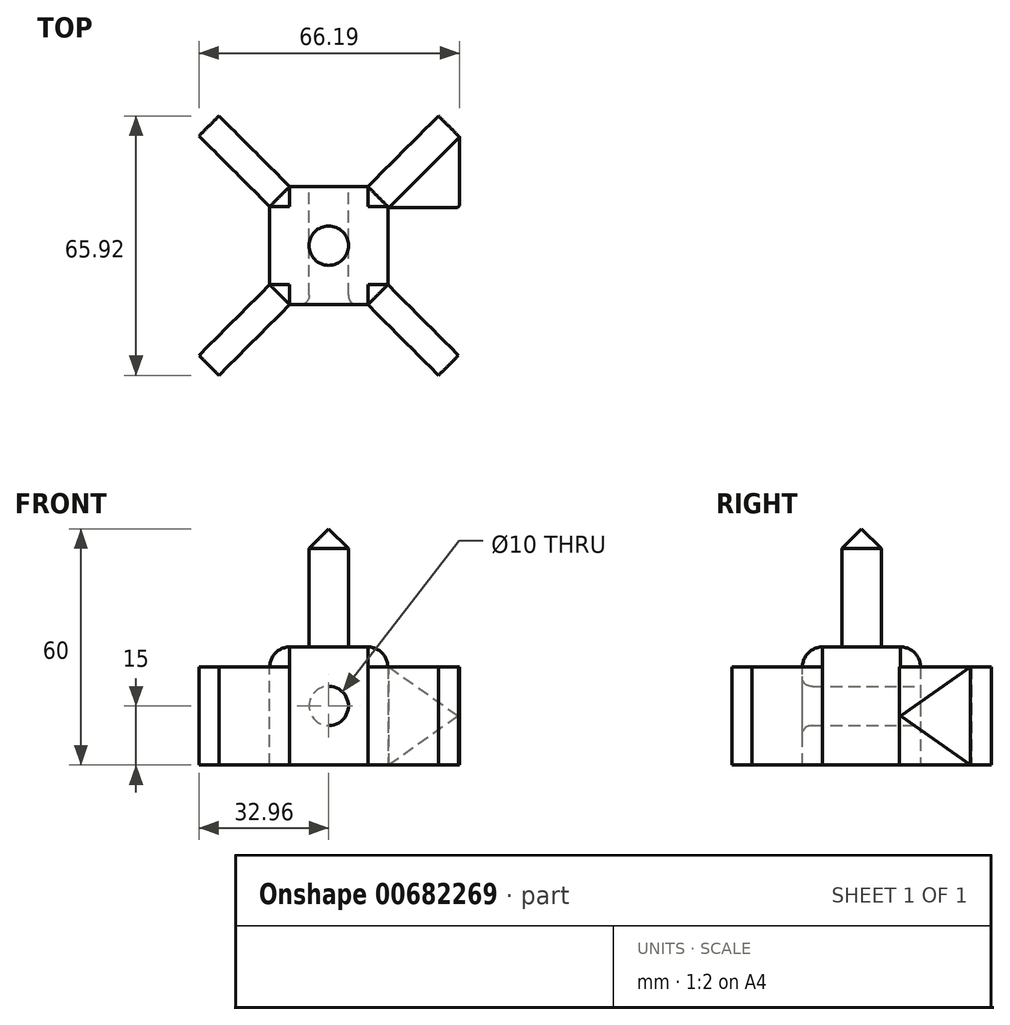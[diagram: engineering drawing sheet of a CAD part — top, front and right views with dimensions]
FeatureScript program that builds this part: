
annotation { "Feature Type Name" : "Feature", "Feature Type Description" : "" }
export const myFeature = defineFeature(function(context is Context, id is Id, definition is map)
    precondition{}
    {
        {
            var Q0;
            Q0=qCreatedBy(makeId("Top.planeOp"),FACE);
            var sketch = newSketch(context, id + "F0", { "sketchPlane" : qUnion([Q0])});
            skLineSegment(sketch, "E0.bottom", {"start": v(15, 15) * mm, "end": v(-15, 15) * mm});
            skLineSegment(sketch, "E0.top", {"start": v(15, -15) * mm, "end": v(-15, -15) * mm});
            skLineSegment(sketch, "E0.left", {"start": v(15, 15) * mm, "end": v(15, -15) * mm});
            skLineSegment(sketch, "E0.right", {"start": v(-15, 15) * mm, "end": v(-15, -15) * mm});
            skPoint(sketch, "E0.middle", {"position": v(0, 0) * mm});
            skSolve(sketch);
        }
        {
            var Q0;
            Q0=makeQuery(id+"F0.imprint","IMPRINT",FACE,{"disambiguationData":[TD([[makeQuery(id+"F0.imprint","IMPRINT",EDGE,{"derivedFrom":sQuery(id+"F0.wireOp",EDGE,"E0.bottom")}),1.0]])]});
            extrude(context, id + "F1", {"entities" : qUnion([Q0]), "depth" : 30 * mm, "offsetDistance" : 25.4 * mm});
        }
        {
            var Q0;
            Q0=makeQuery(id+"F1.opExtrude","SWEPT_BODY",BODY,{"disambiguationData":[OSD([sQuery(id+"F0.wireOp",EDGE,"E0.bottom"),sQuery(id+"F0.wireOp",EDGE,"E0.top"),sQuery(id+"F0.wireOp",EDGE,"E0.left"),sQuery(id+"F0.wireOp",EDGE,"E0.right")])]});
            transform(context, id + "F2", {"entities" : qUnion([Q0]), "transformType" : TransformType.TRANSLATION_3D, "dx" : 0 * mm, "dy" : 0 * mm, "dz" : -15 * mm, "makeCopy" : false});
        }
        {
            var Q0;
            Q0=makeQuery(id+"F1.opExtrude","CAP_FACE",FACE,{"disambiguationData":[OSD([sQuery(id+"F0.wireOp",EDGE,"E0.bottom"),sQuery(id+"F0.wireOp",EDGE,"E0.top"),sQuery(id+"F0.wireOp",EDGE,"E0.left"),sQuery(id+"F0.wireOp",EDGE,"E0.right")])],"isStart":false});
            var sketch = newSketch(context, id + "F3", { "sketchPlane" : qUnion([Q0])});
            skCircle(sketch, "E1", {"center": v(0, 0) * mm, "radius": 5 * mm});
            skSolve(sketch);
        }
        {
            var Q0;
            Q0 = qSketchRegion(id + "F3", true);
            extrude(context, id + "F4", {"entities" : qUnion([Q0]), "operationType" : NewBodyOperationType.ADD, "depth" : 30 * mm, "offsetDistance" : 25.4 * mm});
        }
        {
            var Q0;
            Q0=makeQuery(id+"F1.opExtrude","SWEPT_FACE",FACE,{"disambiguationData":[OSD([sQuery(id+"F0.wireOp",EDGE,"E0.bottom")])]});
            var sketch = newSketch(context, id + "F5", { "sketchPlane" : qUnion([Q0])});
            skCircle(sketch, "E2", {"center": v(0, 0) * mm, "radius": 5 * mm});
            skSolve(sketch);
        }
        {
            var Q0;
            Q0 = qSketchRegion(id + "F5", true);
            extrude(context, id + "F6", {"entities" : qUnion([Q0]), "operationType" : NewBodyOperationType.REMOVE, "oppositeDirection" : true, "depth" : 36.32 * mm, "offsetDistance" : 25.4 * mm});
        }
        {
            var Q0;
            Q0=makeQuery(id+"F1.opExtrude","CAP_EDGE",EDGE,{"disambiguationData":[OSD([sQuery(id+"F0.wireOp",EDGE,"E0.top")])],"isStart":false});
            var Q1;
            Q1=makeQuery(id+"F1.opExtrude","CAP_EDGE",EDGE,{"disambiguationData":[OSD([sQuery(id+"F0.wireOp",EDGE,"E0.left")])],"isStart":false});
            var Q2;
            Q2=makeQuery(id+"F1.opExtrude","CAP_EDGE",EDGE,{"disambiguationData":[OSD([sQuery(id+"F0.wireOp",EDGE,"E0.right")])],"isStart":false});
            var Q3;
            Q3=makeQuery(id+"F1.opExtrude","CAP_EDGE",EDGE,{"disambiguationData":[OSD([sQuery(id+"F0.wireOp",EDGE,"E0.bottom")])],"isStart":false});
            fillet(context, id + "F7", {"entities" : qUnion([Q0, Q1, Q2, Q3]), "radius" : 5.08 * mm, "tangentPropagation" : true, "allowEdgeOverflow" : false});
        }
        {
            var Q0;
            Q0=makeQuery(id+"F4.opExtrude","CAP_EDGE",EDGE,{"disambiguationData":[OSD([sQuery(id+"F3.wireOp",EDGE,"E1")])],"isStart":false});
            chamfer(context, id + "F8", {"entities" : qUnion([Q0]), "chamferType" : ChamferType.OFFSET_ANGLE, "width" : 5 * mm, "oppositeDirection" : true, "angle" : 45 * degree, "tangentPropagation" : true});
        }
        {
            var Q0;
            Q0=makeQuery(id+"F1.opExtrude","SWEPT_EDGE",EDGE,{"disambiguationData":[OSD([sQuery(id+"F0.wireOp",EDGE,"E0.bottom"),sQuery(id+"F0.wireOp",EDGE,"E0.left")])]});
            var Q1;
            Q1=makeQuery(id+"F1.opExtrude","SWEPT_EDGE",EDGE,{"disambiguationData":[OSD([sQuery(id+"F0.wireOp",EDGE,"E0.bottom"),sQuery(id+"F0.wireOp",EDGE,"E0.right")])]});
            var Q2;
            Q2=makeQuery(id+"F1.opExtrude","SWEPT_EDGE",EDGE,{"disambiguationData":[OSD([sQuery(id+"F0.wireOp",EDGE,"E0.top"),sQuery(id+"F0.wireOp",EDGE,"E0.right")])]});
            var Q3;
            Q3=makeQuery(id+"F1.opExtrude","SWEPT_EDGE",EDGE,{"disambiguationData":[OSD([sQuery(id+"F0.wireOp",EDGE,"E0.top"),sQuery(id+"F0.wireOp",EDGE,"E0.left")])]});
            chamfer(context, id + "F9", {"entities" : qUnion([Q0, Q1, Q2, Q3]), "width" : 5.08 * mm, "tangentPropagation" : true});
        }
        {
            var Q0;
            Q0=makeQuery(id+"F6.boolean.opBoolean","INTERSECT",EDGE,{"derivedFrom":[makeQuery(id+"F1.opExtrude","SWEPT_FACE",FACE,{"disambiguationData":[OSD([sQuery(id+"F0.wireOp",EDGE,"E0.top")])]}),makeQuery(id+"F6.opExtrude","SWEPT_FACE",FACE,{"disambiguationData":[OSD([sQuery(id+"F5.wireOp",EDGE,"E2")])]})]});
            var Q1;
            Q1=makeQuery(id+"F6.boolean.opBoolean","COPY",EDGE,{"derivedFrom":makeQuery(id+"F6.opExtrude","CAP_EDGE",EDGE,{"disambiguationData":[OSD([sQuery(id+"F5.wireOp",EDGE,"E2")])],"isStart":true})});
            fillet(context, id + "F10", {"entities" : qUnion([Q0, Q1]), "radius" : 2.5 * mm, "tangentPropagation" : true, "rho" : 0.5, "crossSection" : FilletCrossSection.CONIC, "allowEdgeOverflow" : false});
        }
        {
            var Q0;
            {var subQ0=sQuery(id+"F0.wireOp",EDGE,"E0.left");var subQ1=sQuery(id+"F0.wireOp",EDGE,"E0.bottom");Q0=makeQuery(id+"F9.opChamfer","BLEND_FACE",FACE,{"disambiguationData":[OSD([subQ1,subQ0]),TDD([makeQuery(id+"F1.opExtrude","SWEPT_EDGE",EDGE,{"disambiguationData":[OSD([subQ1,subQ0])]})])]});}
            extrude(context, id + "F11", {"entities" : qUnion([Q0]), "operationType" : NewBodyOperationType.ADD, "depth" : 25.4 * mm, "offsetDistance" : 25.4 * mm});
        }
        {
            var Q0;
            {var subQ0=sQuery(id+"F0.wireOp",EDGE,"E0.left");var subQ1=sQuery(id+"F0.wireOp",EDGE,"E0.top");Q0=makeQuery(id+"F9.opChamfer","BLEND_FACE",FACE,{"disambiguationData":[OSD([subQ1,subQ0]),TDD([makeQuery(id+"F1.opExtrude","SWEPT_EDGE",EDGE,{"disambiguationData":[OSD([subQ1,subQ0])]})])]});}
            extrude(context, id + "F12", {"entities" : qUnion([Q0]), "operationType" : NewBodyOperationType.ADD, "depth" : 25.4 * mm, "offsetDistance" : 25.4 * mm});
        }
        {
            var Q0;
            {var subQ0=sQuery(id+"F0.wireOp",EDGE,"E0.right");var subQ1=sQuery(id+"F0.wireOp",EDGE,"E0.top");Q0=makeQuery(id+"F9.opChamfer","BLEND_FACE",FACE,{"disambiguationData":[OSD([subQ1,subQ0]),TDD([makeQuery(id+"F1.opExtrude","SWEPT_EDGE",EDGE,{"disambiguationData":[OSD([subQ1,subQ0])]})])]});}
            extrude(context, id + "F13", {"entities" : qUnion([Q0]), "operationType" : NewBodyOperationType.ADD, "depth" : 25.4 * mm, "offsetDistance" : 25.4 * mm});
        }
        {
            var Q0;
            {var subQ0=sQuery(id+"F0.wireOp",EDGE,"E0.right");var subQ1=sQuery(id+"F0.wireOp",EDGE,"E0.bottom");Q0=makeQuery(id+"F9.opChamfer","BLEND_FACE",FACE,{"disambiguationData":[OSD([subQ1,subQ0]),TDD([makeQuery(id+"F1.opExtrude","SWEPT_EDGE",EDGE,{"disambiguationData":[OSD([subQ1,subQ0])]})])]});}
            extrude(context, id + "F14", {"entities" : qUnion([Q0]), "operationType" : NewBodyOperationType.ADD, "depth" : 25.4 * mm, "offsetDistance" : 25.4 * mm});
        }
        {
            var Q0;
            {var subQ0=sQuery(id+"F0.wireOp",EDGE,"E0.left");var subQ1=sQuery(id+"F0.wireOp",EDGE,"E0.bottom");Q0=makeQuery(id+"F11.opExtrude","SWEPT_FACE",FACE,{"disambiguationData":[OSD([subQ1,subQ0]),TDD([makeQuery(id+"F9.opChamfer","BLEND_EDGE",EDGE,{"blendedFrom":[makeQuery(id+"F1.opExtrude","SWEPT_EDGE",EDGE,{"disambiguationData":[OSD([subQ1,subQ0])]}),makeQuery(id+"F1.opExtrude","SWEPT_FACE",FACE,{"disambiguationData":[OSD([subQ0])]})],"blendedInto":[makeQuery(id+"F1.opExtrude","SWEPT_FACE",FACE,{"disambiguationData":[OSD([subQ0])]})]})])]});}
            extrude(context, id + "F15", {"entities" : qUnion([Q0]), "operationType" : NewBodyOperationType.ADD, "depth" : 12.7 * mm, "offsetDistance" : 25.4 * mm});
        }
        {
            var Q0;
            Q0=makeQuery(id+"F15.opExtrude","CAP_FACE",FACE,{"disambiguationData":[OSD([sQuery(id+"F0.wireOp",EDGE,"E0.bottom"),sQuery(id+"F0.wireOp",EDGE,"E0.left")])],"isStart":false});
            chamfer(context, id + "F16", {"entities" : qUnion([Q0]), "width" : 12.32 * mm, "tangentPropagation" : true});
        }
    });
